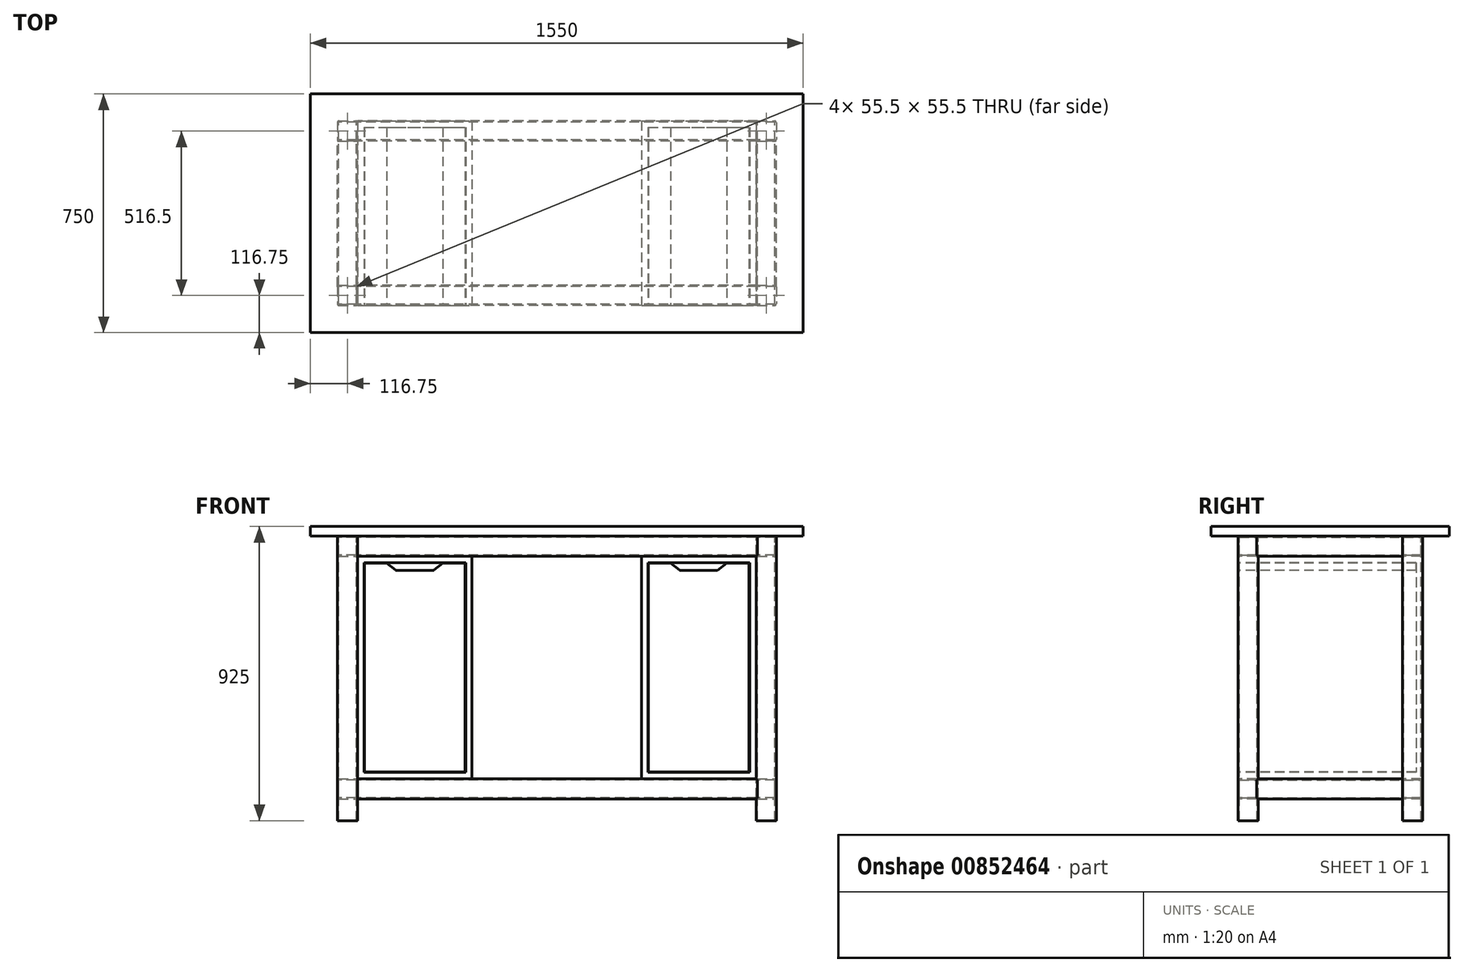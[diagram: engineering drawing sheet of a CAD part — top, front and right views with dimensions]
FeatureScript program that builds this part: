
annotation { "Feature Type Name" : "Feature", "Feature Type Description" : "" }
export const myFeature = defineFeature(function(context is Context, id is Id, definition is map)
    precondition{}
    {
        {
            var Q0;
            Q0=qCreatedBy(makeId("Top.planeOp"),FACE);
            var sketch = newSketch(context, id + "F0", { "sketchPlane" : qUnion([Q0])});
            skPoint(sketch, "E0.middle", {"position": v(0, 0) * mm});
            skLineSegment(sketch, "E1.bottom", {"start": v(-690, 290) * mm, "end": v(690, 290) * mm, "construction": true});
            skLineSegment(sketch, "E1.top", {"start": v(-690, -290) * mm, "end": v(690, -290) * mm, "construction": true});
            skLineSegment(sketch, "E1.left", {"start": v(-690, 290) * mm, "end": v(-690, -290) * mm, "construction": true});
            skLineSegment(sketch, "E1.right", {"start": v(690, 290) * mm, "end": v(690, -290) * mm, "construction": true});
            skLineSegment(sketch, "E2.bottom", {"start": v(-685, 290) * mm, "end": v(-631.5, 290) * mm});
            skLineSegment(sketch, "E2.top", {"start": v(-685, 226.5) * mm, "end": v(-631.5, 226.5) * mm});
            skLineSegment(sketch, "E2.left", {"start": v(-690, 285) * mm, "end": v(-690, 231.5) * mm});
            skLineSegment(sketch, "E2.right", {"start": v(-626.5, 285) * mm, "end": v(-626.5, 231.5) * mm});
            skLineSegment(sketch, "E3.bottom", {"start": v(-630.5, 230.5) * mm, "end": v(-686, 230.5) * mm});
            skLineSegment(sketch, "E3.top", {"start": v(-630.5, 286) * mm, "end": v(-686, 286) * mm});
            skLineSegment(sketch, "E3.left", {"start": v(-630.5, 230.5) * mm, "end": v(-630.5, 286) * mm});
            skLineSegment(sketch, "E3.right", {"start": v(-686, 230.5) * mm, "end": v(-686, 286) * mm});
            skPoint(sketch, "E3.middle", {"position": v(-658.25, 258.25) * mm});
            skPoint(sketch, "E4.visualSharp", {"position": v(-626.5, 226.5) * mm});
            skArc(sketch, "E4.filletArc", {"start": v(-631.5, 226.5) * mm, "mid": v(-627.96, 227.96) * mm, "end": v(-626.5, 231.5) * mm});
            skPoint(sketch, "E5.visualSharp", {"position": v(-690, 226.5) * mm});
            skArc(sketch, "E5.filletArc", {"start": v(-690, 231.5) * mm, "mid": v(-688.54, 227.96) * mm, "end": v(-685, 226.5) * mm});
            skPoint(sketch, "E6.visualSharp", {"position": v(-626.5, 290) * mm});
            skArc(sketch, "E6.filletArc", {"start": v(-626.5, 285) * mm, "mid": v(-627.96, 288.54) * mm, "end": v(-631.5, 290) * mm});
            skPoint(sketch, "E7.visualSharp", {"position": v(-690, 290) * mm});
            skArc(sketch, "E7.filletArc", {"start": v(-685, 290) * mm, "mid": v(-688.54, 288.54) * mm, "end": v(-690, 285) * mm});
            skLineSegment(sketch, "E8.bottom", {"start": v(631.5, 290) * mm, "end": v(685, 290) * mm});
            skLineSegment(sketch, "E8.top", {"start": v(631.5, 226.5) * mm, "end": v(685, 226.5) * mm});
            skLineSegment(sketch, "E8.left", {"start": v(626.5, 285) * mm, "end": v(626.5, 231.5) * mm});
            skLineSegment(sketch, "E8.right", {"start": v(690, 285) * mm, "end": v(690, 231.5) * mm});
            skLineSegment(sketch, "E9.bottom", {"start": v(686, 230.5) * mm, "end": v(630.5, 230.5) * mm});
            skLineSegment(sketch, "E9.top", {"start": v(686, 286) * mm, "end": v(630.5, 286) * mm});
            skLineSegment(sketch, "E9.left", {"start": v(686, 230.5) * mm, "end": v(686, 286) * mm});
            skLineSegment(sketch, "E9.right", {"start": v(630.5, 230.5) * mm, "end": v(630.5, 286) * mm});
            skPoint(sketch, "E9.middle", {"position": v(658.25, 258.25) * mm});
            skPoint(sketch, "E10.visualSharp", {"position": v(690, 226.5) * mm});
            skArc(sketch, "E10.filletArc", {"start": v(685, 226.5) * mm, "mid": v(688.54, 227.96) * mm, "end": v(690, 231.5) * mm});
            skPoint(sketch, "E11.visualSharp", {"position": v(626.5, 226.5) * mm});
            skArc(sketch, "E11.filletArc", {"start": v(626.5, 231.5) * mm, "mid": v(627.96, 227.96) * mm, "end": v(631.5, 226.5) * mm});
            skPoint(sketch, "E12.visualSharp", {"position": v(690, 290) * mm});
            skArc(sketch, "E12.filletArc", {"start": v(690, 285) * mm, "mid": v(688.54, 288.54) * mm, "end": v(685, 290) * mm});
            skPoint(sketch, "E13.visualSharp", {"position": v(626.5, 290) * mm});
            skArc(sketch, "E13.filletArc", {"start": v(631.5, 290) * mm, "mid": v(627.96, 288.54) * mm, "end": v(626.5, 285) * mm});
            skLineSegment(sketch, "E14.bottom", {"start": v(631.5, -226.5) * mm, "end": v(685, -226.5) * mm});
            skLineSegment(sketch, "E14.top", {"start": v(631.5, -290) * mm, "end": v(685, -290) * mm});
            skLineSegment(sketch, "E14.left", {"start": v(626.5, -231.5) * mm, "end": v(626.5, -285) * mm});
            skLineSegment(sketch, "E14.right", {"start": v(690, -231.5) * mm, "end": v(690, -285) * mm});
            skLineSegment(sketch, "E15.bottom", {"start": v(686, -286) * mm, "end": v(630.5, -286) * mm});
            skLineSegment(sketch, "E15.top", {"start": v(686, -230.5) * mm, "end": v(630.5, -230.5) * mm});
            skLineSegment(sketch, "E15.left", {"start": v(686, -286) * mm, "end": v(686, -230.5) * mm});
            skLineSegment(sketch, "E15.right", {"start": v(630.5, -286) * mm, "end": v(630.5, -230.5) * mm});
            skPoint(sketch, "E15.middle", {"position": v(658.25, -258.25) * mm});
            skPoint(sketch, "E16.visualSharp", {"position": v(690, -290) * mm});
            skArc(sketch, "E16.filletArc", {"start": v(685, -290) * mm, "mid": v(688.54, -288.54) * mm, "end": v(690, -285) * mm});
            skPoint(sketch, "E17.visualSharp", {"position": v(626.5, -290) * mm});
            skArc(sketch, "E17.filletArc", {"start": v(626.5, -285) * mm, "mid": v(627.96, -288.54) * mm, "end": v(631.5, -290) * mm});
            skPoint(sketch, "E18.visualSharp", {"position": v(690, -226.5) * mm});
            skArc(sketch, "E18.filletArc", {"start": v(690, -231.5) * mm, "mid": v(688.54, -227.96) * mm, "end": v(685, -226.5) * mm});
            skPoint(sketch, "E19.visualSharp", {"position": v(626.5, -226.5) * mm});
            skArc(sketch, "E19.filletArc", {"start": v(631.5, -226.5) * mm, "mid": v(627.96, -227.96) * mm, "end": v(626.5, -231.5) * mm});
            skLineSegment(sketch, "E20.bottom", {"start": v(-685, -226.5) * mm, "end": v(-631.5, -226.5) * mm});
            skLineSegment(sketch, "E20.top", {"start": v(-685, -290) * mm, "end": v(-631.5, -290) * mm});
            skLineSegment(sketch, "E20.left", {"start": v(-690, -231.5) * mm, "end": v(-690, -285) * mm});
            skLineSegment(sketch, "E20.right", {"start": v(-626.5, -231.5) * mm, "end": v(-626.5, -285) * mm});
            skLineSegment(sketch, "E21.bottom", {"start": v(-630.5, -286) * mm, "end": v(-686, -286) * mm});
            skLineSegment(sketch, "E21.top", {"start": v(-630.5, -230.5) * mm, "end": v(-686, -230.5) * mm});
            skLineSegment(sketch, "E21.left", {"start": v(-630.5, -286) * mm, "end": v(-630.5, -230.5) * mm});
            skLineSegment(sketch, "E21.right", {"start": v(-686, -286) * mm, "end": v(-686, -230.5) * mm});
            skPoint(sketch, "E21.middle", {"position": v(-658.25, -258.25) * mm});
            skPoint(sketch, "E22.visualSharp", {"position": v(-626.5, -290) * mm});
            skArc(sketch, "E22.filletArc", {"start": v(-631.5, -290) * mm, "mid": v(-627.96, -288.54) * mm, "end": v(-626.5, -285) * mm});
            skPoint(sketch, "E23.visualSharp", {"position": v(-690, -290) * mm});
            skArc(sketch, "E23.filletArc", {"start": v(-690, -285) * mm, "mid": v(-688.54, -288.54) * mm, "end": v(-685, -290) * mm});
            skPoint(sketch, "E24.visualSharp", {"position": v(-626.5, -226.5) * mm});
            skArc(sketch, "E24.filletArc", {"start": v(-626.5, -231.5) * mm, "mid": v(-627.96, -227.96) * mm, "end": v(-631.5, -226.5) * mm});
            skPoint(sketch, "E25.visualSharp", {"position": v(-690, -226.5) * mm});
            skArc(sketch, "E25.filletArc", {"start": v(-685, -226.5) * mm, "mid": v(-688.54, -227.96) * mm, "end": v(-690, -231.5) * mm});
            skSolve(sketch);
        }
        {
            var Q0;
            Q0=makeQuery(id+"F0.imprint","IMPRINT",FACE,{"disambiguationData":[TD([[makeQuery(id+"F0.imprint","IMPRINT",EDGE,{"derivedFrom":sQuery(id+"F0.wireOp",EDGE,"E14.bottom")}),-1.0]])]});
            var Q1;
            Q1=makeQuery(id+"F0.imprint","IMPRINT",FACE,{"disambiguationData":[TD([[makeQuery(id+"F0.imprint","IMPRINT",EDGE,{"derivedFrom":sQuery(id+"F0.wireOp",EDGE,"E8.bottom")}),-1.0]])]});
            var Q2;
            Q2=makeQuery(id+"F0.imprint","IMPRINT",FACE,{"disambiguationData":[TD([[makeQuery(id+"F0.imprint","IMPRINT",EDGE,{"derivedFrom":sQuery(id+"F0.wireOp",EDGE,"E2.bottom")}),-1.0]])]});
            var Q3;
            Q3=makeQuery(id+"F0.imprint","IMPRINT",FACE,{"disambiguationData":[TD([[makeQuery(id+"F0.imprint","IMPRINT",EDGE,{"derivedFrom":sQuery(id+"F0.wireOp",EDGE,"E20.bottom")}),-1.0]])]});
            extrude(context, id + "F1", {"entities" : qUnion([Q0, Q1, Q2, Q3]), "oppositeDirection" : true, "depth" : 895 * mm, "offsetDistance" : 25 * mm});
        }
        {
            var Q0;
            Q0=qCreatedBy(makeId("Top.planeOp"),FACE);
            var sketch = newSketch(context, id + "F2", { "sketchPlane" : qUnion([Q0])});
            skLineSegment(sketch, "E26.bottom", {"start": v(-775, 375) * mm, "end": v(775, 375) * mm});
            skLineSegment(sketch, "E26.top", {"start": v(-775, -375) * mm, "end": v(775, -375) * mm});
            skLineSegment(sketch, "E26.left", {"start": v(-775, 375) * mm, "end": v(-775, -375) * mm});
            skLineSegment(sketch, "E26.right", {"start": v(775, 375) * mm, "end": v(775, -375) * mm});
            skPoint(sketch, "E26.middle", {"position": v(0, 0) * mm});
            skSolve(sketch);
        }
        {
            var Q0;
            Q0 = qSketchRegion(id + "F2", true);
            extrude(context, id + "F3", {"entities" : qUnion([Q0]), "depth" : 30 * mm, "offsetDistance" : 25 * mm});
        }
        {
            var Q0;
            Q0=makeQuery(id+"F1.opExtrude","SWEPT_FACE",FACE,{"disambiguationData":[OSD([sQuery(id+"F0.wireOp",EDGE,"E20.right")])]});
            var sketch = newSketch(context, id + "F4", { "sketchPlane" : qUnion([Q0])});
            skLineSegment(sketch, "E27.bottom", {"start": v(-285, 0) * mm, "end": v(-231.5, 0) * mm});
            skLineSegment(sketch, "E27.top", {"start": v(-285, -63.5) * mm, "end": v(-231.5, -63.5) * mm});
            skLineSegment(sketch, "E27.left", {"start": v(-290, -5) * mm, "end": v(-290, -58.5) * mm});
            skLineSegment(sketch, "E27.right", {"start": v(-226.5, -5) * mm, "end": v(-226.5, -58.5) * mm});
            skLineSegment(sketch, "E28.bottom", {"start": v(-230.5, -59.5) * mm, "end": v(-286, -59.5) * mm});
            skLineSegment(sketch, "E28.top", {"start": v(-230.5, -4) * mm, "end": v(-286, -4) * mm});
            skLineSegment(sketch, "E28.left", {"start": v(-230.5, -59.5) * mm, "end": v(-230.5, -4) * mm});
            skLineSegment(sketch, "E28.right", {"start": v(-286, -59.5) * mm, "end": v(-286, -4) * mm});
            skPoint(sketch, "E28.middle", {"position": v(-258.25, -31.75) * mm});
            skPoint(sketch, "E29.visualSharp", {"position": v(-226.5, -63.5) * mm});
            skArc(sketch, "E29.filletArc", {"start": v(-231.5, -63.5) * mm, "mid": v(-227.96, -62.04) * mm, "end": v(-226.5, -58.5) * mm});
            skPoint(sketch, "E30.visualSharp", {"position": v(-290, -63.5) * mm});
            skArc(sketch, "E30.filletArc", {"start": v(-290, -58.5) * mm, "mid": v(-288.54, -62.04) * mm, "end": v(-285, -63.5) * mm});
            skPoint(sketch, "E31.visualSharp", {"position": v(-226.5, 0) * mm});
            skArc(sketch, "E31.filletArc", {"start": v(-226.5, -5) * mm, "mid": v(-227.96, -1.46) * mm, "end": v(-231.5, 0) * mm});
            skPoint(sketch, "E32.visualSharp", {"position": v(-290, 0) * mm});
            skArc(sketch, "E32.filletArc", {"start": v(-285, 0) * mm, "mid": v(-288.54, -1.46) * mm, "end": v(-290, -5) * mm});
            skLineSegment(sketch, "E33.bottom", {"start": v(231.5, 0) * mm, "end": v(285, 0) * mm});
            skLineSegment(sketch, "E33.top", {"start": v(231.5, -63.5) * mm, "end": v(285, -63.5) * mm});
            skLineSegment(sketch, "E33.left", {"start": v(226.5, -5) * mm, "end": v(226.5, -58.5) * mm});
            skLineSegment(sketch, "E33.right", {"start": v(290, -5) * mm, "end": v(290, -58.5) * mm});
            skLineSegment(sketch, "E34.bottom", {"start": v(286, -59.5) * mm, "end": v(230.5, -59.5) * mm});
            skLineSegment(sketch, "E34.top", {"start": v(286, -4) * mm, "end": v(230.5, -4) * mm});
            skLineSegment(sketch, "E34.left", {"start": v(286, -59.5) * mm, "end": v(286, -4) * mm});
            skLineSegment(sketch, "E34.right", {"start": v(230.5, -59.5) * mm, "end": v(230.5, -4) * mm});
            skPoint(sketch, "E34.middle", {"position": v(258.25, -31.75) * mm});
            skPoint(sketch, "E35.visualSharp", {"position": v(290, -63.5) * mm});
            skArc(sketch, "E35.filletArc", {"start": v(285, -63.5) * mm, "mid": v(288.54, -62.04) * mm, "end": v(290, -58.5) * mm});
            skPoint(sketch, "E36.visualSharp", {"position": v(226.5, -63.5) * mm});
            skArc(sketch, "E36.filletArc", {"start": v(226.5, -58.5) * mm, "mid": v(227.96, -62.04) * mm, "end": v(231.5, -63.5) * mm});
            skPoint(sketch, "E37.visualSharp", {"position": v(290, 0) * mm});
            skArc(sketch, "E37.filletArc", {"start": v(290, -5) * mm, "mid": v(288.54, -1.46) * mm, "end": v(285, 0) * mm});
            skPoint(sketch, "E38.visualSharp", {"position": v(226.5, 0) * mm});
            skArc(sketch, "E38.filletArc", {"start": v(231.5, 0) * mm, "mid": v(227.96, -1.46) * mm, "end": v(226.5, -5) * mm});
            skLineSegment(sketch, "E39.bottom", {"start": v(231.5, -763.5) * mm, "end": v(285, -763.5) * mm});
            skLineSegment(sketch, "E39.top", {"start": v(231.5, -827) * mm, "end": v(285, -827) * mm});
            skLineSegment(sketch, "E39.left", {"start": v(226.5, -768.5) * mm, "end": v(226.5, -822) * mm});
            skLineSegment(sketch, "E39.right", {"start": v(290, -768.5) * mm, "end": v(290, -822) * mm});
            skLineSegment(sketch, "E40.bottom", {"start": v(286, -823) * mm, "end": v(230.5, -823) * mm});
            skLineSegment(sketch, "E40.top", {"start": v(286, -767.5) * mm, "end": v(230.5, -767.5) * mm});
            skLineSegment(sketch, "E40.left", {"start": v(286, -823) * mm, "end": v(286, -767.5) * mm});
            skLineSegment(sketch, "E40.right", {"start": v(230.5, -823) * mm, "end": v(230.5, -767.5) * mm});
            skPoint(sketch, "E40.middle", {"position": v(258.25, -795.25) * mm});
            skPoint(sketch, "E41.visualSharp", {"position": v(290, -827) * mm});
            skArc(sketch, "E41.filletArc", {"start": v(285, -827) * mm, "mid": v(288.54, -825.54) * mm, "end": v(290, -822) * mm});
            skPoint(sketch, "E42.visualSharp", {"position": v(226.5, -827) * mm});
            skArc(sketch, "E42.filletArc", {"start": v(226.5, -822) * mm, "mid": v(227.96, -825.54) * mm, "end": v(231.5, -827) * mm});
            skPoint(sketch, "E43.visualSharp", {"position": v(290, -763.5) * mm});
            skArc(sketch, "E43.filletArc", {"start": v(290, -768.5) * mm, "mid": v(288.54, -764.96) * mm, "end": v(285, -763.5) * mm});
            skPoint(sketch, "E44.visualSharp", {"position": v(226.5, -763.5) * mm});
            skArc(sketch, "E44.filletArc", {"start": v(231.5, -763.5) * mm, "mid": v(227.96, -764.96) * mm, "end": v(226.5, -768.5) * mm});
            skLineSegment(sketch, "E45.bottom", {"start": v(-285, -763.5) * mm, "end": v(-231.5, -763.5) * mm});
            skLineSegment(sketch, "E45.top", {"start": v(-285, -827) * mm, "end": v(-231.5, -827) * mm});
            skLineSegment(sketch, "E45.left", {"start": v(-290, -768.5) * mm, "end": v(-290, -822) * mm});
            skLineSegment(sketch, "E45.right", {"start": v(-226.5, -768.5) * mm, "end": v(-226.5, -822) * mm});
            skLineSegment(sketch, "E46.bottom", {"start": v(-230.5, -823) * mm, "end": v(-286, -823) * mm});
            skLineSegment(sketch, "E46.top", {"start": v(-230.5, -767.5) * mm, "end": v(-286, -767.5) * mm});
            skLineSegment(sketch, "E46.left", {"start": v(-230.5, -823) * mm, "end": v(-230.5, -767.5) * mm});
            skLineSegment(sketch, "E46.right", {"start": v(-286, -823) * mm, "end": v(-286, -767.5) * mm});
            skPoint(sketch, "E46.middle", {"position": v(-258.25, -795.25) * mm});
            skPoint(sketch, "E47.visualSharp", {"position": v(-226.5, -827) * mm});
            skArc(sketch, "E47.filletArc", {"start": v(-231.5, -827) * mm, "mid": v(-227.96, -825.54) * mm, "end": v(-226.5, -822) * mm});
            skPoint(sketch, "E48.visualSharp", {"position": v(-290, -827) * mm});
            skArc(sketch, "E48.filletArc", {"start": v(-290, -822) * mm, "mid": v(-288.54, -825.54) * mm, "end": v(-285, -827) * mm});
            skPoint(sketch, "E49.visualSharp", {"position": v(-226.5, -763.5) * mm});
            skArc(sketch, "E49.filletArc", {"start": v(-226.5, -768.5) * mm, "mid": v(-227.96, -764.96) * mm, "end": v(-231.5, -763.5) * mm});
            skPoint(sketch, "E50.visualSharp", {"position": v(-290, -763.5) * mm});
            skArc(sketch, "E50.filletArc", {"start": v(-285, -763.5) * mm, "mid": v(-288.54, -764.96) * mm, "end": v(-290, -768.5) * mm});
            skSolve(sketch);
        }
        {
            var Q0;
            Q0 = qSketchRegion(id + "F4", true);
            extrude(context, id + "F5", {"entities" : qUnion([Q0]), "endBound" : BoundingType.UP_TO_NEXT, "depth" : 25 * mm, "offsetDistance" : 25 * mm});
        }
        {
            var Q0;
            Q0=makeQuery(id+"F1.opExtrude","SWEPT_FACE",FACE,{"disambiguationData":[OSD([sQuery(id+"F0.wireOp",EDGE,"E2.top")])]});
            var sketch = newSketch(context, id + "F6", { "sketchPlane" : qUnion([Q0])});
            skLineSegment(sketch, "E51.bottom", {"start": v(-685, 0) * mm, "end": v(-631.5, 0) * mm});
            skLineSegment(sketch, "E51.top", {"start": v(-685, -63.5) * mm, "end": v(-631.5, -63.5) * mm});
            skLineSegment(sketch, "E51.left", {"start": v(-690, -5) * mm, "end": v(-690, -58.5) * mm});
            skLineSegment(sketch, "E51.right", {"start": v(-626.5, -5) * mm, "end": v(-626.5, -58.5) * mm});
            skLineSegment(sketch, "E52.bottom", {"start": v(-630.5, -59.5) * mm, "end": v(-686, -59.5) * mm});
            skLineSegment(sketch, "E52.top", {"start": v(-630.5, -4) * mm, "end": v(-686, -4) * mm});
            skLineSegment(sketch, "E52.left", {"start": v(-630.5, -59.5) * mm, "end": v(-630.5, -4) * mm});
            skLineSegment(sketch, "E52.right", {"start": v(-686, -59.5) * mm, "end": v(-686, -4) * mm});
            skPoint(sketch, "E52.middle", {"position": v(-658.25, -31.75) * mm});
            skPoint(sketch, "E53.visualSharp", {"position": v(-626.5, -63.5) * mm});
            skArc(sketch, "E53.filletArc", {"start": v(-631.5, -63.5) * mm, "mid": v(-627.96, -62.04) * mm, "end": v(-626.5, -58.5) * mm});
            skPoint(sketch, "E54.visualSharp", {"position": v(-690, -63.5) * mm});
            skArc(sketch, "E54.filletArc", {"start": v(-690, -58.5) * mm, "mid": v(-688.54, -62.04) * mm, "end": v(-685, -63.5) * mm});
            skPoint(sketch, "E55.visualSharp", {"position": v(-626.5, 0) * mm});
            skArc(sketch, "E55.filletArc", {"start": v(-626.5, -5) * mm, "mid": v(-627.96, -1.46) * mm, "end": v(-631.5, 0) * mm});
            skPoint(sketch, "E56.visualSharp", {"position": v(-690, 0) * mm});
            skArc(sketch, "E56.filletArc", {"start": v(-685, 0) * mm, "mid": v(-688.54, -1.46) * mm, "end": v(-690, -5) * mm});
            skLineSegment(sketch, "E57.bottom", {"start": v(631.5, 0) * mm, "end": v(685, 0) * mm});
            skLineSegment(sketch, "E57.top", {"start": v(631.5, -63.5) * mm, "end": v(685, -63.5) * mm});
            skLineSegment(sketch, "E57.left", {"start": v(626.5, -5) * mm, "end": v(626.5, -58.5) * mm});
            skLineSegment(sketch, "E57.right", {"start": v(690, -5) * mm, "end": v(690, -58.5) * mm});
            skLineSegment(sketch, "E58.bottom", {"start": v(686, -59.5) * mm, "end": v(630.5, -59.5) * mm});
            skLineSegment(sketch, "E58.top", {"start": v(686, -4) * mm, "end": v(630.5, -4) * mm});
            skLineSegment(sketch, "E58.left", {"start": v(686, -59.5) * mm, "end": v(686, -4) * mm});
            skLineSegment(sketch, "E58.right", {"start": v(630.5, -59.5) * mm, "end": v(630.5, -4) * mm});
            skPoint(sketch, "E58.middle", {"position": v(658.25, -31.75) * mm});
            skPoint(sketch, "E59.visualSharp", {"position": v(690, -63.5) * mm});
            skArc(sketch, "E59.filletArc", {"start": v(685, -63.5) * mm, "mid": v(688.54, -62.04) * mm, "end": v(690, -58.5) * mm});
            skPoint(sketch, "E60.visualSharp", {"position": v(626.5, -63.5) * mm});
            skArc(sketch, "E60.filletArc", {"start": v(626.5, -58.5) * mm, "mid": v(627.96, -62.04) * mm, "end": v(631.5, -63.5) * mm});
            skPoint(sketch, "E61.visualSharp", {"position": v(690, 0) * mm});
            skArc(sketch, "E61.filletArc", {"start": v(690, -5) * mm, "mid": v(688.54, -1.46) * mm, "end": v(685, 0) * mm});
            skPoint(sketch, "E62.visualSharp", {"position": v(626.5, 0) * mm});
            skArc(sketch, "E62.filletArc", {"start": v(631.5, 0) * mm, "mid": v(627.96, -1.46) * mm, "end": v(626.5, -5) * mm});
            skLineSegment(sketch, "E63.bottom", {"start": v(-685, -763.5) * mm, "end": v(-631.5, -763.5) * mm});
            skLineSegment(sketch, "E63.top", {"start": v(-685, -827) * mm, "end": v(-631.5, -827) * mm});
            skLineSegment(sketch, "E63.left", {"start": v(-690, -768.5) * mm, "end": v(-690, -822) * mm});
            skLineSegment(sketch, "E63.right", {"start": v(-626.5, -768.5) * mm, "end": v(-626.5, -822) * mm});
            skLineSegment(sketch, "E64.bottom", {"start": v(-630.5, -823) * mm, "end": v(-686, -823) * mm});
            skLineSegment(sketch, "E64.top", {"start": v(-630.5, -767.5) * mm, "end": v(-686, -767.5) * mm});
            skLineSegment(sketch, "E64.left", {"start": v(-630.5, -823) * mm, "end": v(-630.5, -767.5) * mm});
            skLineSegment(sketch, "E64.right", {"start": v(-686, -823) * mm, "end": v(-686, -767.5) * mm});
            skPoint(sketch, "E64.middle", {"position": v(-658.25, -795.25) * mm});
            skPoint(sketch, "E65.visualSharp", {"position": v(-626.5, -827) * mm});
            skArc(sketch, "E65.filletArc", {"start": v(-631.5, -827) * mm, "mid": v(-627.96, -825.54) * mm, "end": v(-626.5, -822) * mm});
            skPoint(sketch, "E66.visualSharp", {"position": v(-690, -827) * mm});
            skArc(sketch, "E66.filletArc", {"start": v(-690, -822) * mm, "mid": v(-688.54, -825.54) * mm, "end": v(-685, -827) * mm});
            skPoint(sketch, "E67.visualSharp", {"position": v(-626.5, -763.5) * mm});
            skArc(sketch, "E67.filletArc", {"start": v(-626.5, -768.5) * mm, "mid": v(-627.96, -764.96) * mm, "end": v(-631.5, -763.5) * mm});
            skPoint(sketch, "E68.visualSharp", {"position": v(-690, -763.5) * mm});
            skArc(sketch, "E68.filletArc", {"start": v(-685, -763.5) * mm, "mid": v(-688.54, -764.96) * mm, "end": v(-690, -768.5) * mm});
            skLineSegment(sketch, "E69.bottom", {"start": v(631.5, -763.5) * mm, "end": v(685, -763.5) * mm});
            skLineSegment(sketch, "E69.top", {"start": v(631.5, -827) * mm, "end": v(685, -827) * mm});
            skLineSegment(sketch, "E69.left", {"start": v(626.5, -768.5) * mm, "end": v(626.5, -822) * mm});
            skLineSegment(sketch, "E69.right", {"start": v(690, -768.5) * mm, "end": v(690, -822) * mm});
            skLineSegment(sketch, "E70.bottom", {"start": v(686, -823) * mm, "end": v(630.5, -823) * mm});
            skLineSegment(sketch, "E70.top", {"start": v(686, -767.5) * mm, "end": v(630.5, -767.5) * mm});
            skLineSegment(sketch, "E70.left", {"start": v(686, -823) * mm, "end": v(686, -767.5) * mm});
            skLineSegment(sketch, "E70.right", {"start": v(630.5, -823) * mm, "end": v(630.5, -767.5) * mm});
            skPoint(sketch, "E70.middle", {"position": v(658.25, -795.25) * mm});
            skPoint(sketch, "E71.visualSharp", {"position": v(690, -827) * mm});
            skArc(sketch, "E71.filletArc", {"start": v(685, -827) * mm, "mid": v(688.54, -825.54) * mm, "end": v(690, -822) * mm});
            skPoint(sketch, "E72.visualSharp", {"position": v(626.5, -827) * mm});
            skArc(sketch, "E72.filletArc", {"start": v(626.5, -822) * mm, "mid": v(627.96, -825.54) * mm, "end": v(631.5, -827) * mm});
            skPoint(sketch, "E73.visualSharp", {"position": v(690, -763.5) * mm});
            skArc(sketch, "E73.filletArc", {"start": v(690, -768.5) * mm, "mid": v(688.54, -764.96) * mm, "end": v(685, -763.5) * mm});
            skPoint(sketch, "E74.visualSharp", {"position": v(626.5, -763.5) * mm});
            skArc(sketch, "E74.filletArc", {"start": v(631.5, -763.5) * mm, "mid": v(627.96, -764.96) * mm, "end": v(626.5, -768.5) * mm});
            skSolve(sketch);
        }
        {
            var Q0;
            Q0 = qSketchRegion(id + "F6", true);
            extrude(context, id + "F7", {"entities" : qUnion([Q0]), "endBound" : BoundingType.UP_TO_NEXT, "depth" : 25 * mm, "offsetDistance" : 25 * mm});
        }
        {
            var Q0;
            Q0=makeQuery(id+"F1.opExtrude","SWEPT_FACE",FACE,{"disambiguationData":[OSD([sQuery(id+"F0.wireOp",EDGE,"E20.top")])]});
            var sketch = newSketch(context, id + "F8", { "sketchPlane" : qUnion([Q0])});
            skLineSegment(sketch, "E75.bottom", {"start": v(-626.5, -63.5) * mm, "end": v(-266.5, -63.5) * mm});
            skLineSegment(sketch, "E75.top", {"start": v(-626.5, -763.5) * mm, "end": v(-266.5, -763.5) * mm});
            skLineSegment(sketch, "E75.left", {"start": v(-626.5, -63.5) * mm, "end": v(-626.5, -763.5) * mm});
            skLineSegment(sketch, "E75.right", {"start": v(-266.5, -63.5) * mm, "end": v(-266.5, -763.5) * mm});
            skLineSegment(sketch, "E76.bottom", {"start": v(266.5, -63.5) * mm, "end": v(626.5, -63.5) * mm});
            skLineSegment(sketch, "E76.top", {"start": v(266.5, -763.5) * mm, "end": v(626.5, -763.5) * mm});
            skLineSegment(sketch, "E76.left", {"start": v(266.5, -63.5) * mm, "end": v(266.5, -763.5) * mm});
            skLineSegment(sketch, "E76.right", {"start": v(626.5, -63.5) * mm, "end": v(626.5, -763.5) * mm});
            skLineSegment(sketch, "E77.bottom", {"start": v(-606.5, -83.5) * mm, "end": v(-286.5, -83.5) * mm});
            skLineSegment(sketch, "E77.top", {"start": v(-606.5, -743.5) * mm, "end": v(-286.5, -743.5) * mm});
            skLineSegment(sketch, "E77.left", {"start": v(-606.5, -83.5) * mm, "end": v(-606.5, -743.5) * mm});
            skLineSegment(sketch, "E77.right", {"start": v(-286.5, -83.5) * mm, "end": v(-286.5, -743.5) * mm});
            skLineSegment(sketch, "E78.bottom", {"start": v(-604.5, -85.5) * mm, "end": v(-534.5, -85.5) * mm});
            skLineSegment(sketch, "E78.top", {"start": v(-604.5, -741.5) * mm, "end": v(-288.5, -741.5) * mm});
            skLineSegment(sketch, "E78.left", {"start": v(-604.5, -85.5) * mm, "end": v(-604.5, -741.5) * mm});
            skLineSegment(sketch, "E78.right", {"start": v(-288.5, -85.5) * mm, "end": v(-288.5, -741.5) * mm});
            skLineSegment(sketch, "E79", {"start": v(-534.5, -85.5) * mm, "end": v(-534.5, -85.5) * mm});
            skLineSegment(sketch, "E80", {"start": v(-503.74, -108.5) * mm, "end": v(-389.26, -108.5) * mm});
            skLineSegment(sketch, "E81", {"start": v(-386.15, -107.42) * mm, "end": v(-358.5, -85.5) * mm});
            skPoint(sketch, "E82.visualSharp", {"position": v(-505.48, -108.5) * mm});
            skArc(sketch, "E82.filletArc", {"start": v(-506.85, -107.42) * mm, "mid": v(-505.39, -108.22) * mm, "end": v(-503.74, -108.5) * mm});
            skPoint(sketch, "E83.visualSharp", {"position": v(-387.52, -108.5) * mm});
            skArc(sketch, "E83.filletArc", {"start": v(-389.26, -108.5) * mm, "mid": v(-387.61, -108.22) * mm, "end": v(-386.15, -107.42) * mm});
            skLineSegment(sketch, "E84", {"start": v(-534.5, -85.5) * mm, "end": v(-506.85, -107.42) * mm});
            skLineSegment(sketch, "E85", {"start": v(-358.5, -85.5) * mm, "end": v(-288.5, -85.5) * mm});
            skLineSegment(sketch, "E86.bottom", {"start": v(286.5, -83.5) * mm, "end": v(606.5, -83.5) * mm});
            skLineSegment(sketch, "E86.top", {"start": v(286.5, -743.5) * mm, "end": v(606.5, -743.5) * mm});
            skLineSegment(sketch, "E86.left", {"start": v(286.5, -83.5) * mm, "end": v(286.5, -743.5) * mm});
            skLineSegment(sketch, "E86.right", {"start": v(606.5, -83.5) * mm, "end": v(606.5, -743.5) * mm});
            skLineSegment(sketch, "E87.bottom", {"start": v(288.5, -85.5) * mm, "end": v(357.5, -85.5) * mm});
            skLineSegment(sketch, "E87.top", {"start": v(288.5, -741.5) * mm, "end": v(604.5, -741.5) * mm});
            skLineSegment(sketch, "E87.left", {"start": v(288.5, -85.5) * mm, "end": v(288.5, -741.5) * mm});
            skLineSegment(sketch, "E87.right", {"start": v(604.5, -85.5) * mm, "end": v(604.5, -741.5) * mm});
            skLineSegment(sketch, "E88", {"start": v(384.57, -239.53) * mm, "end": v(384.57, -239.53) * mm});
            skLineSegment(sketch, "E89", {"start": v(388.26, -108.5) * mm, "end": v(502.74, -108.5) * mm});
            skLineSegment(sketch, "E90", {"start": v(505.78, -107.47) * mm, "end": v(534.5, -85.5) * mm});
            skPoint(sketch, "E91.visualSharp", {"position": v(386.52, -108.5) * mm});
            skArc(sketch, "E91.filletArc", {"start": v(385.15, -107.42) * mm, "mid": v(386.61, -108.22) * mm, "end": v(388.26, -108.5) * mm});
            skPoint(sketch, "E92.visualSharp", {"position": v(504.43, -108.5) * mm});
            skArc(sketch, "E92.filletArc", {"start": v(502.74, -108.5) * mm, "mid": v(504.35, -108.24) * mm, "end": v(505.78, -107.47) * mm});
            skLineSegment(sketch, "E93", {"start": v(357.5, -85.5) * mm, "end": v(385.15, -107.42) * mm});
            skLineSegment(sketch, "E94", {"start": v(534.5, -85.5) * mm, "end": v(604.5, -85.5) * mm});
            skSolve(sketch);
        }
        {
            var Q0;
            Q0=makeQuery(id+"F8.imprint","IMPRINT",FACE,{"disambiguationData":[TD([[makeQuery(id+"F8.imprint","IMPRINT",EDGE,{"derivedFrom":sQuery(id+"F8.wireOp",EDGE,"E76.bottom")}),-1.0]])]});
            var Q1;
            Q1=makeQuery(id+"F8.imprint","IMPRINT",FACE,{"disambiguationData":[TD([[makeQuery(id+"F8.imprint","IMPRINT",EDGE,{"derivedFrom":sQuery(id+"F8.wireOp",EDGE,"E78.bottom")}),-1.0]])]});
            var Q2;
            Q2=makeQuery(id+"F8.imprint","IMPRINT",FACE,{"disambiguationData":[TD([[makeQuery(id+"F8.imprint","IMPRINT",EDGE,{"derivedFrom":sQuery(id+"F8.wireOp",EDGE,"E75.bottom")}),-1.0]])]});
            var Q3;
            Q3=makeQuery(id+"F8.imprint","IMPRINT",FACE,{"disambiguationData":[TD([[makeQuery(id+"F8.imprint","IMPRINT",EDGE,{"derivedFrom":sQuery(id+"F8.wireOp",EDGE,"E77.bottom")}),-1.0]])]});
            var Q4;
            Q4=makeQuery(id+"F8.imprint","IMPRINT",FACE,{"disambiguationData":[TD([[makeQuery(id+"F8.imprint","IMPRINT",EDGE,{"derivedFrom":sQuery(id+"F8.wireOp",EDGE,"E87.bottom")}),-1.0]])]});
            var Q5;
            Q5=makeQuery(id+"F8.imprint","IMPRINT",FACE,{"disambiguationData":[TD([[makeQuery(id+"F8.imprint","IMPRINT",EDGE,{"derivedFrom":sQuery(id+"F8.wireOp",EDGE,"E86.bottom")}),-1.0]])]});
            extrude(context, id + "F9", {"entities" : qUnion([Q0, Q1, Q2, Q3, Q4, Q5]), "oppositeDirection" : true, "depth" : 580 * mm, "offsetDistance" : 25 * mm});
        }
        {
            var Q0;
            Q0=makeQuery(id+"F8.imprint","IMPRINT",FACE,{"disambiguationData":[TD([[makeQuery(id+"F8.imprint","IMPRINT",EDGE,{"derivedFrom":sQuery(id+"F8.wireOp",EDGE,"E77.bottom")}),-1.0]])]});
            var Q1;
            Q1=makeQuery(id+"F8.imprint","IMPRINT",FACE,{"disambiguationData":[TD([[makeQuery(id+"F8.imprint","IMPRINT",EDGE,{"derivedFrom":sQuery(id+"F8.wireOp",EDGE,"E86.bottom")}),-1.0]])]});
            extrude(context, id + "F10", {"entities" : qUnion([Q0, Q1]), "operationType" : NewBodyOperationType.REMOVE, "oppositeDirection" : true, "depth" : 560 * mm, "offsetDistance" : 25 * mm});
        }
        {
            var Q0;
            Q0=makeQuery(id+"F8.imprint","IMPRINT",FACE,{"disambiguationData":[TD([[makeQuery(id+"F8.imprint","IMPRINT",EDGE,{"derivedFrom":sQuery(id+"F8.wireOp",EDGE,"E86.bottom")}),-1.0]])]});
            extrude(context, id + "F11", {"entities" : qUnion([Q0]), "operationType" : NewBodyOperationType.REMOVE, "oppositeDirection" : true, "depth" : 560 * mm, "offsetDistance" : 25 * mm});
        }
    });
